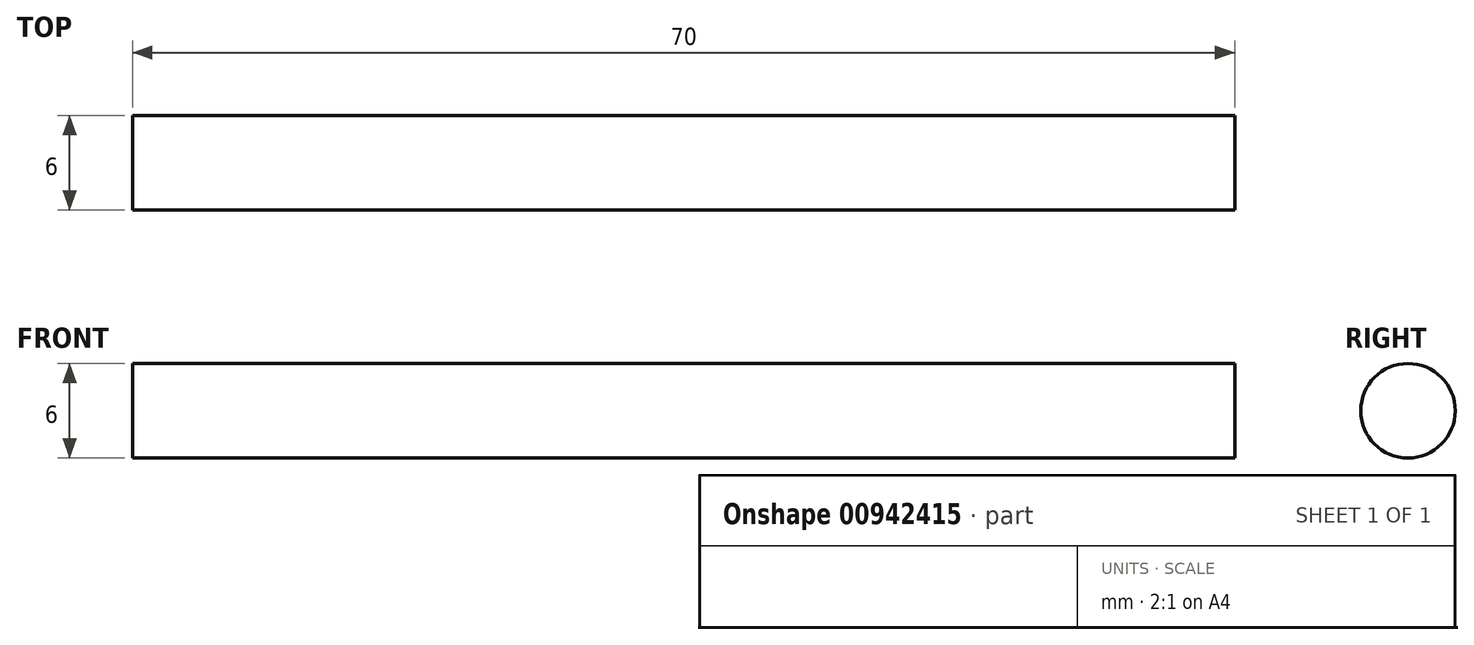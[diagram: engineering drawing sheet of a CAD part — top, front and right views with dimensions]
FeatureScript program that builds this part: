
annotation { "Feature Type Name" : "Feature", "Feature Type Description" : "" }
export const myFeature = defineFeature(function(context is Context, id is Id, definition is map)
    precondition{}
    {
        {
            var Q0;
            Q0=qCreatedBy(makeId("Right.planeOp"),FACE);
            var sketch = newSketch(context, id + "F0", { "sketchPlane" : qUnion([Q0])});
            skCircle(sketch, "E0", {"center": v(0, 0) * mm, "radius": 3 * mm});
            skSolve(sketch);
        }
        {
            var Q0;
            Q0=makeQuery(id+"F0.imprint","IMPRINT",FACE,{"disambiguationData":[TD([[makeQuery(id+"F0.imprint","IMPRINT",EDGE,{"derivedFrom":sQuery(id+"F0.wireOp",EDGE,"E0")}),1.0]])]});
            extrude(context, id + "F1", {"entities" : qUnion([Q0]), "depth" : 70 * mm, "offsetDistance" : 25 * mm});
        }
    });
